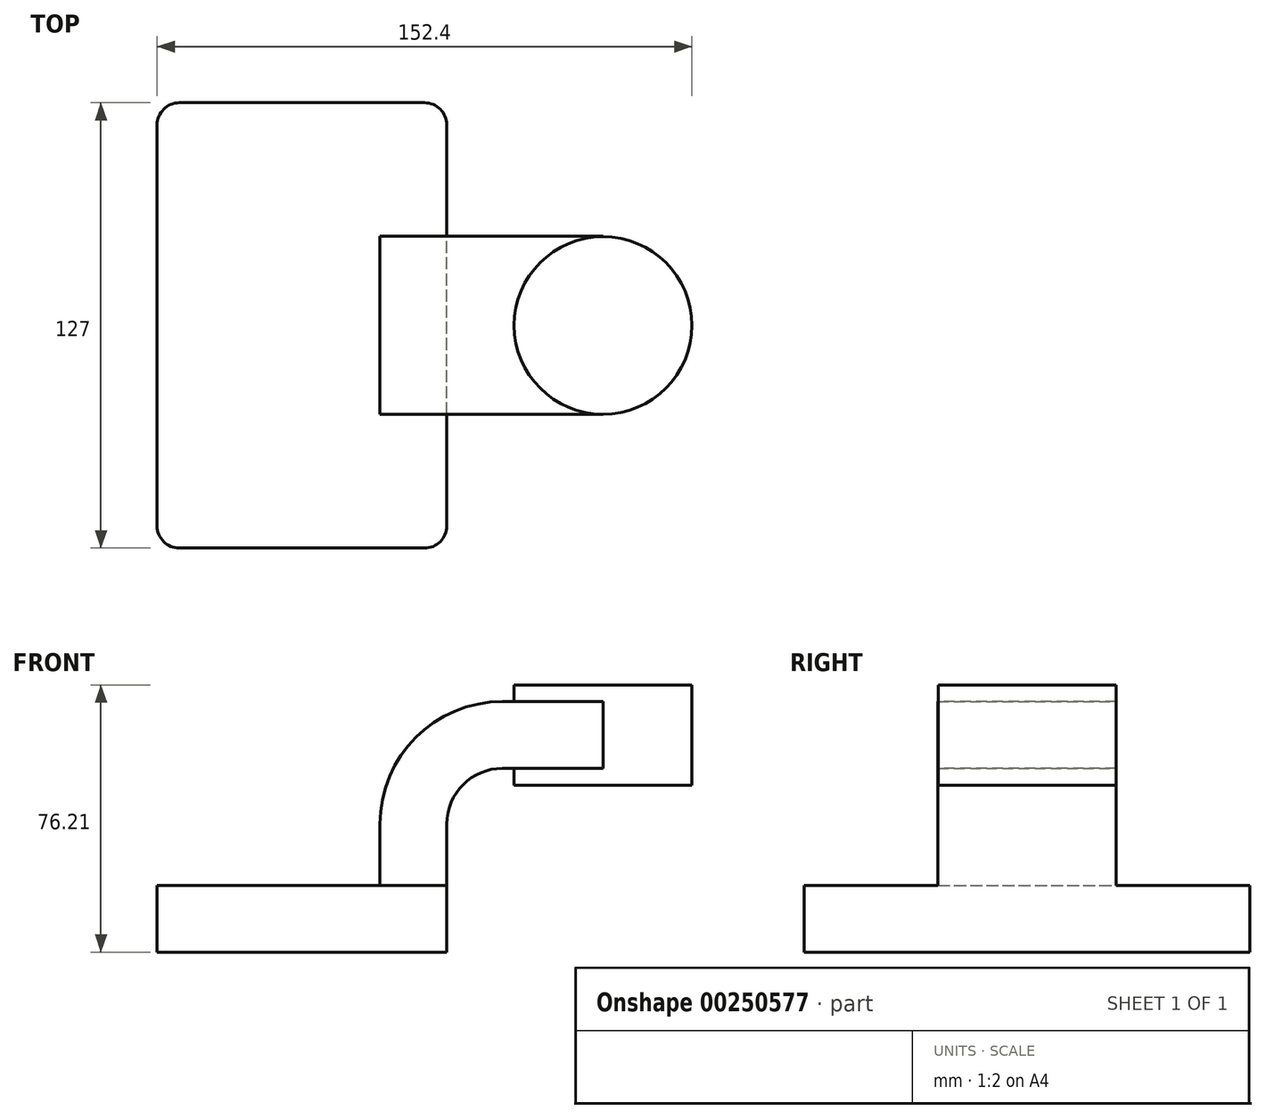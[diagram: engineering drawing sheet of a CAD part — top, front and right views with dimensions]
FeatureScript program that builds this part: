
annotation { "Feature Type Name" : "Feature", "Feature Type Description" : "" }
export const myFeature = defineFeature(function(context is Context, id is Id, definition is map)
    precondition{}
    {
        {
            var Q0;
            Q0=qCreatedBy(makeId("Front.planeOp"),FACE);
            var sketch = newSketch(context, id + "F0", { "sketchPlane" : qUnion([Q0])});
            skLineSegment(sketch, "E0.bottom", {"start": v(41.27, 9.53) * mm, "end": v(-41.28, 9.53) * mm});
            skLineSegment(sketch, "E0.top", {"start": v(41.28, -9.52) * mm, "end": v(-41.27, -9.52) * mm});
            skLineSegment(sketch, "E0.left", {"start": v(41.28, 9.53) * mm, "end": v(41.28, -9.52) * mm});
            skLineSegment(sketch, "E0.right", {"start": v(-41.28, 9.53) * mm, "end": v(-41.27, -9.52) * mm});
            skPoint(sketch, "E0.middle", {"position": v(0, 0) * mm});
            skLineSegment(sketch, "E1.bottom", {"start": v(60.33, 66.68) * mm, "end": v(111.13, 66.68) * mm});
            skLineSegment(sketch, "E1.top", {"start": v(60.33, 38.1) * mm, "end": v(111.13, 38.1) * mm});
            skLineSegment(sketch, "E1.left", {"start": v(60.33, 66.68) * mm, "end": v(60.33, 38.1) * mm});
            skLineSegment(sketch, "E1.right", {"start": v(111.13, 66.68) * mm, "end": v(111.13, 38.1) * mm});
            skPoint(sketch, "E1.middle", {"position": v(85.73, 52.39) * mm});
            skLineSegment(sketch, "E2", {"start": v(41.27, 9.53) * mm, "end": v(41.27, 27) * mm});
            skArc(sketch, "E3", {"start": v(41.27, 27) * mm, "mid": v(45.92, 38.23) * mm, "end": v(57.15, 42.88) * mm});
            skLineSegment(sketch, "E4", {"start": v(57.15, 42.88) * mm, "end": v(88.17, 42.88) * mm});
            skLineSegment(sketch, "E5.0", {"start": v(57.15, 61.93) * mm, "end": v(85.8, 61.93) * mm});
            skArc(sketch, "E5.1", {"start": v(22.23, 27) * mm, "mid": v(32.45, 51.7) * mm, "end": v(57.15, 61.93) * mm});
            skLineSegment(sketch, "E5.2", {"start": v(22.22, 9.53) * mm, "end": v(22.22, 27) * mm});
            skPoint(sketch, "E6.endSnap0", {"position": v(85.73, 66.68) * mm});
            skFitSpline(sketch, "E7", {"points": [v(-41.28, 9.53) * mm, v(57.15, 61.93) * mm], "startDerivative": vector(0.85, 63.41) * mm, "endDerivative": vector(34.22, -12.75) * mm});
            skLineSegment(sketch, "E8", {"start": v(85.8, 66.68) * mm, "end": v(85.8, 38.1) * mm});
            skSolve(sketch);
        }
        {
            var Q0;
            {var subQ1=sQuery(id+"F0.wireOp",EDGE,"E2");Q0=makeQuery(id+"F0.imprint","IMPRINT",FACE,{"disambiguationData":[TD([[makeQuery(id+"F0.imprint","IMPRINT",EDGE,{"derivedFrom":subQ1}),1.0]])]});}
            var Q1;
            {var subQ5=sQuery(id+"F0.wireOp",EDGE,"NtpG5Anv-j1AK-oJTh-Wb1c-abH5DdRfyxK6");Q1=makeQuery(id+"F0.imprint","IMPRINT",FACE,{"disambiguationData":[TD([[makeQuery(id+"F0.imprint","IMPRINT",EDGE,{"derivedFrom":subQ5}),1.0]])]});}
            var Q2;
            {var subQ0=sQuery(id+"F0.wireOp",EDGE,"E5.0");var subQ1=sQuery(id+"F0.wireOp",EDGE,"E1.left");var subQ2=makeQuery(id+"F0.imprint","INTERSECT",VERTEX,{"derivedFrom":[subQ1,subQ0]});Q2=makeQuery(id+"F0.imprint","IMPRINT",FACE,{"disambiguationData":[TD([[makeQuery(id+"F0.imprint","IMPRINT",EDGE,{"disambiguationData":[TD([[subQ2,-1.0]])],"derivedFrom":subQ1}),1.0]])]});}
            extrude(context, id + "F1", {"entities" : qUnion([Q0, Q1, Q2]), "endBound" : BoundingType.SYMMETRIC, "depth" : 50.8 * mm});
        }
        {
            var Q0;
            Q0=makeQuery(id+"F0.imprint","IMPRINT",FACE,{"disambiguationData":[TD([[makeQuery(id+"F0.imprint","IMPRINT",EDGE,{"derivedFrom":sQuery(id+"F0.wireOp",EDGE,"E0.top")}),-1.0]])]});
            extrude(context, id + "F2", {"entities" : qUnion([Q0]), "operationType" : NewBodyOperationType.ADD, "endBound" : BoundingType.SYMMETRIC, "depth" : 127 * mm});
        }
        {
            var Q0;
            Q0=makeQuery(id+"F0.imprint","IMPRINT",FACE,{"disambiguationData":[TD([[makeQuery(id+"F0.imprint","IMPRINT",EDGE,{"derivedFrom":sQuery(id+"F0.wireOp",EDGE,"E5.1")}),1.0]])]});
            extrude(context, id + "F3", {"entities" : qUnion([Q0]), "operationType" : NewBodyOperationType.ADD, "endBound" : BoundingType.SYMMETRIC, "depth" : 15.88 * mm});
        }
        {
            var Q0;
            {var subQ0=sQuery(id+"F0.wireOp",EDGE,"E1.right");Q0=makeQuery(id+"F0.imprint","IMPRINT",FACE,{"disambiguationData":[TD([[makeQuery(id+"F0.imprint","IMPRINT",EDGE,{"derivedFrom":subQ0}),-1.0]])]});}
            var Q1;
            Q1=sQuery(id+"F0.wireOp",EDGE,"E8");
            revolve(context, id + "F4", {"operationType" : NewBodyOperationType.ADD, "entities" : qUnion([Q0]), "axis" : qUnion([Q1]), "revolveType" : RevolveType.FULL});
        }
        {
            var Q0;
            Q0=makeQuery(id+"F2.opExtrude","CAP_EDGE",EDGE,{"disambiguationData":[OSD([sQuery(id+"F0.wireOp",EDGE,"E0.left")])],"isStart":false});
            var Q1;
            Q1=makeQuery(id+"F2.opExtrude","CAP_EDGE",EDGE,{"disambiguationData":[OSD([sQuery(id+"F0.wireOp",EDGE,"E0.right")])],"isStart":false});
            var Q2;
            Q2=makeQuery(id+"F2.opExtrude","CAP_EDGE",EDGE,{"disambiguationData":[OSD([sQuery(id+"F0.wireOp",EDGE,"E0.left")])],"isStart":true});
            var Q3;
            Q3=makeQuery(id+"F2.opExtrude","CAP_EDGE",EDGE,{"disambiguationData":[OSD([sQuery(id+"F0.wireOp",EDGE,"E0.right")])],"isStart":true});
            fillet(context, id + "F5", {"entities" : qUnion([Q0, Q1, Q2, Q3]), "radius" : 6.35 * mm, "tangentPropagation" : true, "allowEdgeOverflow" : false});
        }
    });
